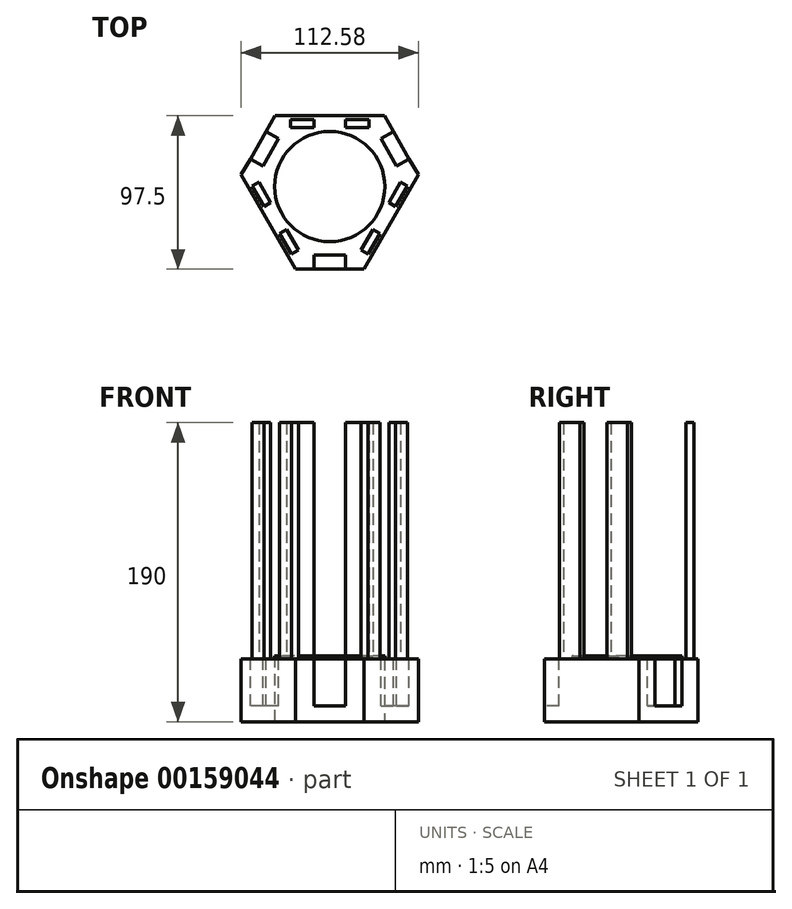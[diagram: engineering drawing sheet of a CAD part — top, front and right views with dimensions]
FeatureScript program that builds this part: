
annotation { "Feature Type Name" : "Feature", "Feature Type Description" : "" }
export const myFeature = defineFeature(function(context is Context, id is Id, definition is map)
    precondition{}
    {
        {
            var Q0;
            Q0=qCreatedBy(makeId("Top.planeOp"),FACE);
            var sketch = newSketch(context, id + "F0", { "sketchPlane" : qUnion([Q0])});
            skCircle(sketch, "E0.cCircle", {"center": v(0, 0) * mm, "radius": 90 * mm, "construction": true});
            skLineSegment(sketch, "E0.0", {"start": v(0, -90) * mm, "end": v(-77.94, 45) * mm});
            skLineSegment(sketch, "E0.1", {"start": v(-77.94, 45) * mm, "end": v(77.94, 45) * mm});
            skLineSegment(sketch, "E0.2", {"start": v(77.94, 45) * mm, "end": v(0, -90) * mm});
            skSolve(sketch);
        }
        {
            var Q0;
            Q0 = qSketchRegion(id + "F0", true);
            extrude(context, id + "F1", {"entities" : qUnion([Q0]), "depth" : 40 * mm});
        }
        {
            var Q0;
            Q0=makeQuery(id+"F1.opExtrude","SWEPT_EDGE",EDGE,{"disambiguationData":[OSD([sQuery(id+"F0.wireOp",EDGE,"E0.0"),sQuery(id+"F0.wireOp",EDGE,"E0.2")])]});
            var Q1;
            Q1=makeQuery(id+"F1.opExtrude","SWEPT_EDGE",EDGE,{"disambiguationData":[OSD([sQuery(id+"F0.wireOp",EDGE,"E0.1"),sQuery(id+"F0.wireOp",EDGE,"E0.2")])]});
            var Q2;
            Q2=makeQuery(id+"F1.opExtrude","SWEPT_EDGE",EDGE,{"disambiguationData":[OSD([sQuery(id+"F0.wireOp",EDGE,"E0.0"),sQuery(id+"F0.wireOp",EDGE,"E0.1")])]});
            chamfer(context, id + "F2", {"entities" : qUnion([Q0, Q1, Q2]), "width" : 25 * mm, "tangentPropagation" : true});
        }
        {
            var Q0;
            Q0=makeQuery(id+"F1.opExtrude","CAP_FACE",FACE,{"disambiguationData":[OSD([sQuery(id+"F0.wireOp",EDGE,"E0.0"),sQuery(id+"F0.wireOp",EDGE,"E0.1"),sQuery(id+"F0.wireOp",EDGE,"E0.2")])],"isStart":false});
            var sketch = newSketch(context, id + "F3", { "sketchPlane" : qUnion([Q0])});
            skLineSegment(sketch, "E1.bottom", {"start": v(-10, -43.35) * mm, "end": v(10, -43.35) * mm});
            skLineSegment(sketch, "E1.top", {"start": v(-10, -63.35) * mm, "end": v(10, -63.35) * mm});
            skLineSegment(sketch, "E1.left", {"start": v(-10, -43.35) * mm, "end": v(-10, -63.35) * mm});
            skLineSegment(sketch, "E1.right", {"start": v(10, -43.35) * mm, "end": v(10, -63.35) * mm});
            skPoint(sketch, "E1.middle", {"position": v(0, -53.35) * mm});
            skLineSegment(sketch, "E2.1.0", {"start": v(-42.54, 13.01) * mm, "end": v(-59.86, 23.01) * mm});
            skPoint(sketch, "E2.1.1", {"position": v(-46.2, 26.67) * mm});
            skLineSegment(sketch, "E2.1.2", {"start": v(-49.86, 40.33) * mm, "end": v(-59.86, 23.01) * mm});
            skLineSegment(sketch, "E2.1.3", {"start": v(-32.54, 30.33) * mm, "end": v(-42.54, 13.01) * mm});
            skLineSegment(sketch, "E2.1.4", {"start": v(-32.54, 30.33) * mm, "end": v(-49.86, 40.33) * mm});
            skLineSegment(sketch, "E2.2.0", {"start": v(32.54, 30.33) * mm, "end": v(49.86, 40.33) * mm});
            skPoint(sketch, "E2.2.1", {"position": v(46.2, 26.67) * mm});
            skLineSegment(sketch, "E2.2.2", {"start": v(59.86, 23.01) * mm, "end": v(49.86, 40.33) * mm});
            skLineSegment(sketch, "E2.2.3", {"start": v(42.54, 13.01) * mm, "end": v(32.54, 30.33) * mm});
            skLineSegment(sketch, "E2.2.4", {"start": v(42.54, 13.01) * mm, "end": v(59.86, 23.01) * mm});
            skPoint(sketch, "E2.center", {"position": v(0, 0) * mm});
            skLineSegment(sketch, "E2.anchor1", {"start": v(0, 0) * mm, "end": v(-10, -63.35) * mm, "construction": true});
            skLineSegment(sketch, "E2.anchor2", {"start": v(0, 0) * mm, "end": v(59.86, 23.01) * mm, "construction": true});
            skSolve(sketch);
        }
        {
            var Q0;
            Q0 = qSketchRegion(id + "F3", true);
            extrude(context, id + "F4", {"entities" : qUnion([Q0]), "operationType" : NewBodyOperationType.REMOVE, "oppositeDirection" : true, "depth" : 30 * mm});
        }
        {
            var Q0;
            Q0=makeQuery(id+"F1.opExtrude","CAP_FACE",FACE,{"disambiguationData":[OSD([sQuery(id+"F0.wireOp",EDGE,"E0.0"),sQuery(id+"F0.wireOp",EDGE,"E0.1"),sQuery(id+"F0.wireOp",EDGE,"E0.2")])],"isStart":false});
            var sketch = newSketch(context, id + "F5", { "sketchPlane" : qUnion([Q0])});
            skLineSegment(sketch, "E3.bottom", {"start": v(-25, 37.5) * mm, "end": v(-10, 37.5) * mm});
            skLineSegment(sketch, "E3.top", {"start": v(-25, 42.5) * mm, "end": v(-10, 42.5) * mm});
            skLineSegment(sketch, "E3.left", {"start": v(-25, 37.5) * mm, "end": v(-25, 42.5) * mm});
            skLineSegment(sketch, "E3.right", {"start": v(25, 37.5) * mm, "end": v(25, 42.5) * mm});
            skPoint(sketch, "E3.middle", {"position": v(0, 40) * mm});
            skLineSegment(sketch, "E4.left", {"start": v(-10, 37.5) * mm, "end": v(-10, 42.5) * mm});
            skLineSegment(sketch, "E4.right", {"start": v(10, 37.5) * mm, "end": v(10, 42.5) * mm});
            skLineSegment(sketch, "E5.trimOffspring", {"start": v(10, 42.5) * mm, "end": v(25, 42.5) * mm});
            skLineSegment(sketch, "E6.trimOffspring", {"start": v(10, 37.5) * mm, "end": v(25, 37.5) * mm});
            skLineSegment(sketch, "E7.1.0", {"start": v(49.3, 0.4) * mm, "end": v(41.8, -12.59) * mm});
            skPoint(sketch, "E7.1.1", {"position": v(34.64, -20) * mm});
            skLineSegment(sketch, "E7.1.2", {"start": v(27.48, -27.41) * mm, "end": v(19.98, -40.4) * mm});
            skLineSegment(sketch, "E7.1.3", {"start": v(31.8, -29.91) * mm, "end": v(24.3, -42.9) * mm});
            skLineSegment(sketch, "E7.1.4", {"start": v(44.98, 2.9) * mm, "end": v(37.48, -10.09) * mm});
            skPoint(sketch, "E7.1.5", {"position": v(34.64, -20) * mm});
            skLineSegment(sketch, "E7.1.6", {"start": v(44.98, 2.9) * mm, "end": v(49.3, 0.4) * mm});
            skLineSegment(sketch, "E7.1.7", {"start": v(19.98, -40.4) * mm, "end": v(24.3, -42.9) * mm});
            skLineSegment(sketch, "E7.1.8", {"start": v(27.48, -27.41) * mm, "end": v(31.8, -29.91) * mm});
            skLineSegment(sketch, "E7.1.9", {"start": v(37.48, -10.09) * mm, "end": v(41.8, -12.59) * mm});
            skLineSegment(sketch, "E7.2.0", {"start": v(-24.3, -42.9) * mm, "end": v(-31.8, -29.91) * mm});
            skPoint(sketch, "E7.2.1", {"position": v(-34.64, -20) * mm});
            skLineSegment(sketch, "E7.2.2", {"start": v(-37.48, -10.09) * mm, "end": v(-44.98, 2.9) * mm});
            skLineSegment(sketch, "E7.2.3", {"start": v(-41.8, -12.59) * mm, "end": v(-49.3, 0.4) * mm});
            skLineSegment(sketch, "E7.2.4", {"start": v(-19.98, -40.4) * mm, "end": v(-27.48, -27.41) * mm});
            skPoint(sketch, "E7.2.5", {"position": v(-34.64, -20) * mm});
            skLineSegment(sketch, "E7.2.6", {"start": v(-19.98, -40.4) * mm, "end": v(-24.3, -42.9) * mm});
            skLineSegment(sketch, "E7.2.7", {"start": v(-44.98, 2.9) * mm, "end": v(-49.3, 0.4) * mm});
            skLineSegment(sketch, "E7.2.8", {"start": v(-37.48, -10.09) * mm, "end": v(-41.8, -12.59) * mm});
            skLineSegment(sketch, "E7.2.9", {"start": v(-27.48, -27.41) * mm, "end": v(-31.8, -29.91) * mm});
            skPoint(sketch, "E7.center", {"position": v(0, 0) * mm});
            skLineSegment(sketch, "E7.anchor1", {"start": v(0, 0) * mm, "end": v(-25, 37.5) * mm, "construction": true});
            skLineSegment(sketch, "E7.anchor2", {"start": v(0, 0) * mm, "end": v(-19.98, -40.4) * mm, "construction": true});
            skSolve(sketch);
        }
        {
            var Q0;
            Q0 = qSketchRegion(id + "F5", true);
            extrude(context, id + "F6", {"entities" : qUnion([Q0]), "operationType" : NewBodyOperationType.ADD, "depth" : 150 * mm});
        }
        {
            var Q0;
            Q0=makeQuery(id+"F1.opExtrude","CAP_FACE",FACE,{"disambiguationData":[OSD([sQuery(id+"F0.wireOp",EDGE,"E0.0"),sQuery(id+"F0.wireOp",EDGE,"E0.1"),sQuery(id+"F0.wireOp",EDGE,"E0.2")])],"isStart":false});
            var sketch = newSketch(context, id + "F7", { "sketchPlane" : qUnion([Q0])});
            skCircle(sketch, "E8", {"center": v(0, 0) * mm, "radius": 35 * mm});
            skSolve(sketch);
        }
        {
            var Q0;
            Q0 = qSketchRegion(id + "F7", true);
            extrude(context, id + "F8", {"entities" : qUnion([Q0]), "operationType" : NewBodyOperationType.ADD, "depth" : 2 * mm});
        }
    });
